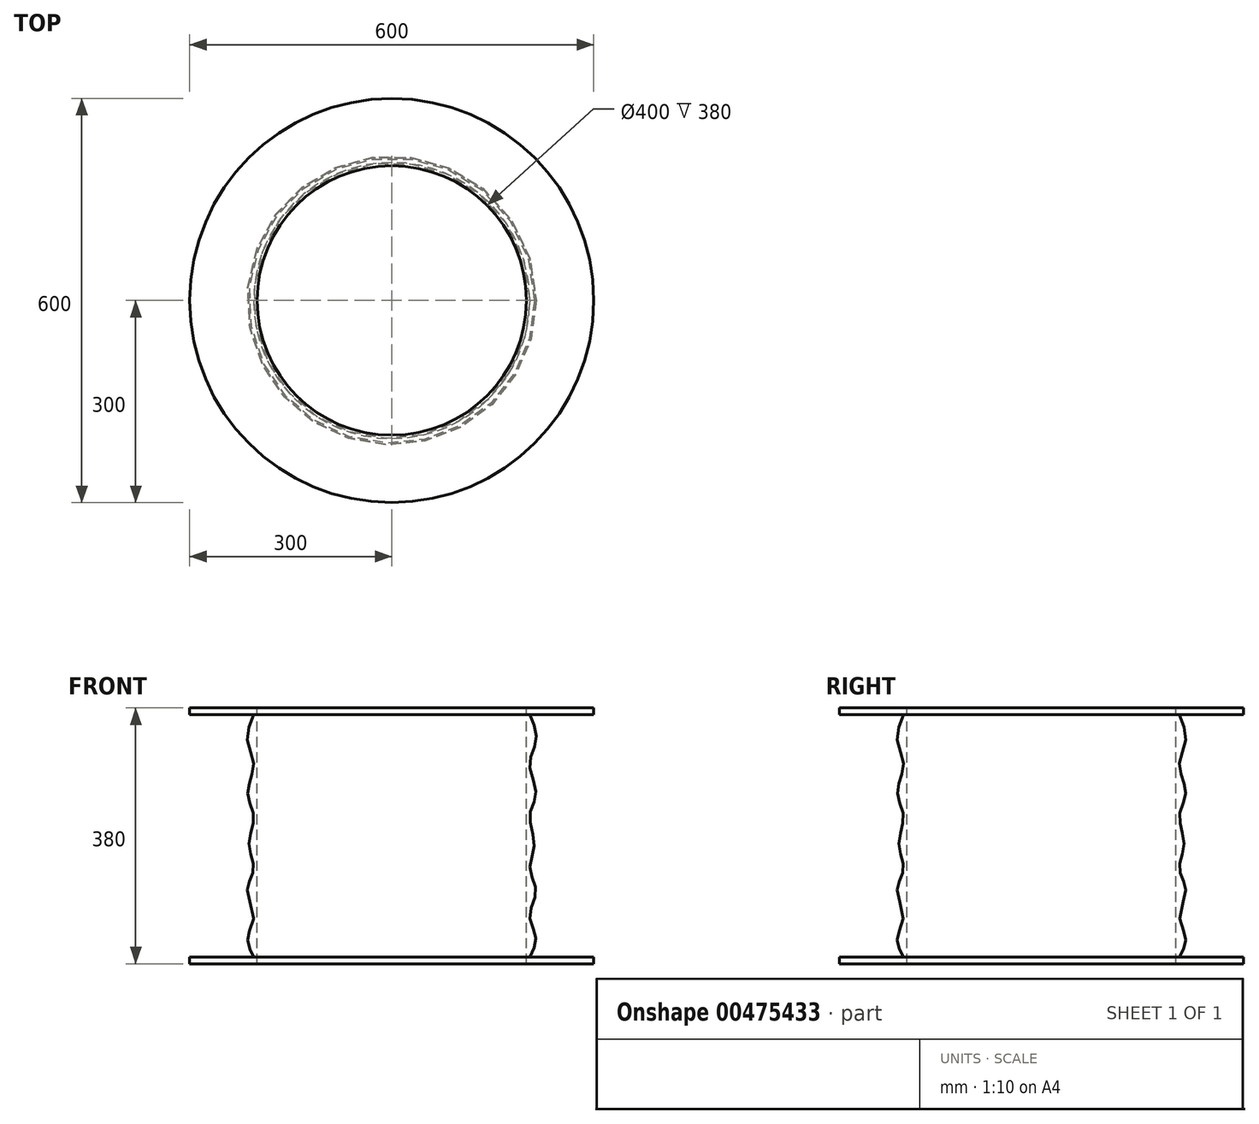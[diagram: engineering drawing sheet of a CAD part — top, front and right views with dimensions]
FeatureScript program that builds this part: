
annotation { "Feature Type Name" : "Feature", "Feature Type Description" : "" }
export const myFeature = defineFeature(function(context is Context, id is Id, definition is map)
    precondition{}
    {
        {
            var Q0;
            Q0=qCreatedBy(makeId("Front.planeOp"),FACE);
            var sketch = newSketch(context, id + "F0", { "sketchPlane" : qUnion([Q0])});
            skLineSegment(sketch, "E0", {"start": v(0, 122.8) * mm, "end": v(0, -360.56) * mm, "construction": true});
            skLineSegment(sketch, "E1", {"start": v(-200, -81.56) * mm, "end": v(-200, 298.44) * mm});
            skLineSegment(sketch, "E2", {"start": v(-200, 298.44) * mm, "end": v(-300, 298.44) * mm});
            skLineSegment(sketch, "E3", {"start": v(-300, 298.44) * mm, "end": v(-300, 288.44) * mm});
            skLineSegment(sketch, "E4", {"start": v(-300, 288.44) * mm, "end": v(-205, 288.44) * mm});
            skLineSegment(sketch, "E5", {"start": v(-200, -81.56) * mm, "end": v(-300, -81.56) * mm});
            skLineSegment(sketch, "E6", {"start": v(-300, -81.56) * mm, "end": v(-300, -71.56) * mm});
            skLineSegment(sketch, "E7", {"start": v(-300, -71.56) * mm, "end": v(-205, -71.56) * mm});
            skLineSegment(sketch, "E8", {"start": v(-205, 288.44) * mm, "end": v(-205, -71.56) * mm, "construction": true});
            skFitSpline(sketch, "E9", {"points": [v(-205, 288.44) * mm, v(-214.38, 250.98) * mm, v(-205, 214.12) * mm, v(-213.97, 171.47) * mm, v(-205, 137.93) * mm, v(-211.9, 95.28) * mm, v(-205, 59.25) * mm, v(-214.38, 26.95) * mm, v(-205, -9.9) * mm, v(-213.97, -43.03) * mm, v(-205, -71.56) * mm], "startDerivative": vector(-157.96, -370.6) * mm, "endDerivative": vector(166.82, -312.16) * mm});
            skSolve(sketch);
        }
        {
            var Q0;
            Q0 = qSketchRegion(id + "F0", true);
            var Q1;
            Q1=sQuery(id+"F0.wireOp",EDGE,"E0");
            revolve(context, id + "F1", {"entities" : qUnion([Q0]), "axis" : qUnion([Q1]), "revolveType" : RevolveType.FULL});
        }
    });
